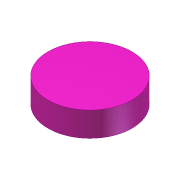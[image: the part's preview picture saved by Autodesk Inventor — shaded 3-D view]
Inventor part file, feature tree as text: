
AUTODESK INVENTOR PART (.ipt)
format: ipt  version: 2012 (Build 160160000, 160)  size: 69,632 bytes
history: native  units: in
note: dims shown in document units (in); Inventor stores cm internally (conversion verified against a paired STEP export)
features: extrude x1, sketch x1
ambient origin geometry x8: Origin, YZ Plane, XZ Plane, XY Plane, X Axis, Y Axis, Z Axis, Center Point
bodies: Solid1 (feature_tree)
feature tree (2):
  extrude  "Extrusion1"  Depth=3.5in TaperAngle=0.0deg
  sketch  "Sketch2"  dims[d0=12.0in d1=3.5in d2=0.0in]
